# Revit family: Sensor-Lutron-Wall_Mount-Occupancy-12ft-LOS-WIR
name_source: partatom
category: Lighting Devices
revit_build: Autodesk Revit 2017 (Build: 20160720_1515(x64)
units: mm (PartAtom-declared; Revit-internal decimal feet)

## family parameters
Cut with Voids When Loaded = No
Host = Face
Maintain Annotation Orientation = Yes
OmniClass Number = 23.85.80.11.27
OmniClass Title = Lighting Controls
Part Type = Normal
Room Calculation Point = No
Round Connector Dimension = Use Diameter
Shared = No

## types (1)
- LOS-WIR-WH
    Assembly Code = D5030800
    Cost = 0 $
    Coverage = 1600.00 SF
    Default Elevation = 6' - 0"
    Description = Infrared Wall Mount Occupancy Sensor
    Field of View = 110.00°
    Height = 0' - 5 1/4"
    Infrared Major Motion = 40' - 0"
    Infrared Minor Motion = 20' - 0"
    Instruction Sheet Link = http://www.lutron.com
    Manufacturer = Lutron Electronics Co., Inc
    Manufacturer Fax Number = 610-282-1243
    Model = LOS-WIR-WH
    Nominal Depth = 0' - 3 29/32"
    Nominal Height = 0' - 6 13/32"
    Nominal Width = 0' - 3 19/32"
    Performance URL = http://www.lutron.com
    Product Documentation Link = http://www.lutron.com
    Product Name = Infrared Wall Mount Occupancy Sensor
    Product Page URL = http://www.lutron.com
    Range Diagram Height = 12' - 0"
    Sensor Material = Plastic-Lutron-White-Gloss
    Series = LOS-W
    URL = http://www.lutron.com
    Version = 2017 - v1.0b
    Video Link = https://www.youtube.com
    Voltage Comments = 20-24VDC
    Warranty URL = http://www.lutron.com

## geometry (parser evidence)
native form markers: Sweep x4
no freeform markers — native parametric forms only
